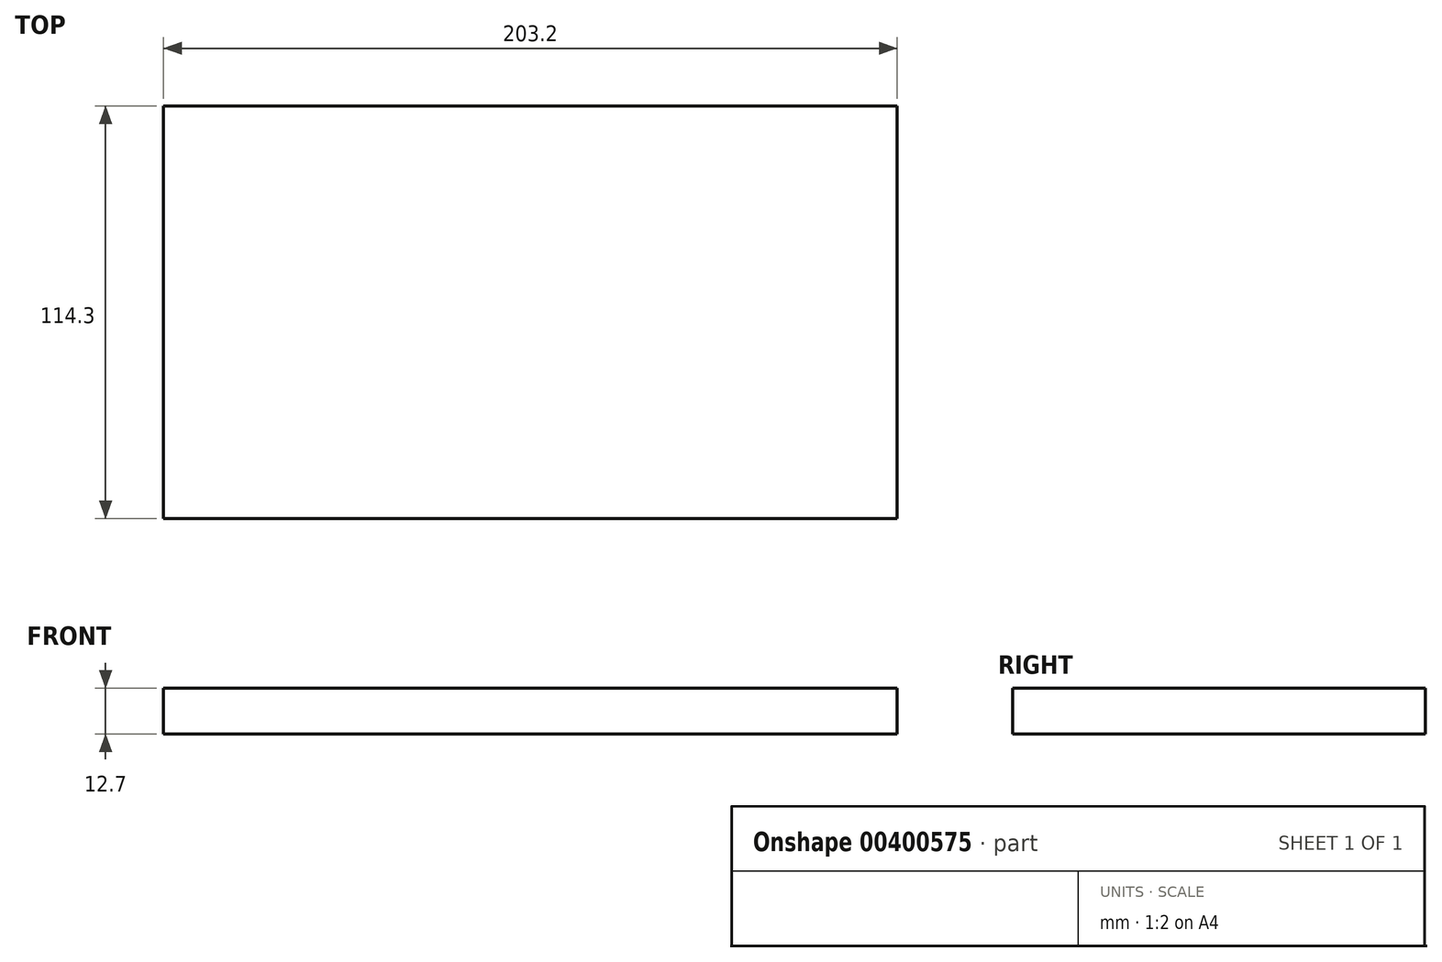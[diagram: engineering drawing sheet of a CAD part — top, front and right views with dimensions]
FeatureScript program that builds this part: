
annotation { "Feature Type Name" : "Feature", "Feature Type Description" : "" }
export const myFeature = defineFeature(function(context is Context, id is Id, definition is map)
    precondition{}
    {
        {
            var Q0;
            Q0=qCreatedBy(makeId("Top.planeOp"),FACE);
            var sketch = newSketch(context, id + "F0", { "sketchPlane" : qUnion([Q0])});
            skLineSegment(sketch, "E0.bottom", {"start": v(101.6, -57.15) * mm, "end": v(-101.6, -57.15) * mm});
            skLineSegment(sketch, "E0.top", {"start": v(101.6, 57.15) * mm, "end": v(-101.6, 57.15) * mm});
            skLineSegment(sketch, "E0.left", {"start": v(101.6, -57.15) * mm, "end": v(101.6, 57.15) * mm});
            skLineSegment(sketch, "E0.right", {"start": v(-101.6, -57.15) * mm, "end": v(-101.6, 57.15) * mm});
            skPoint(sketch, "E0.middle", {"position": v(0, 0) * mm});
            skSolve(sketch);
        }
        {
            var Q0;
            Q0=makeQuery(id+"F0.imprint","IMPRINT",FACE,{"disambiguationData":[TD([[makeQuery(id+"F0.imprint","IMPRINT",EDGE,{"derivedFrom":sQuery(id+"F0.wireOp",EDGE,"E0.bottom")}),-1.0]])]});
            extrude(context, id + "F1", {"entities" : qUnion([Q0]), "depth" : 12.7 * mm});
        }
    });
